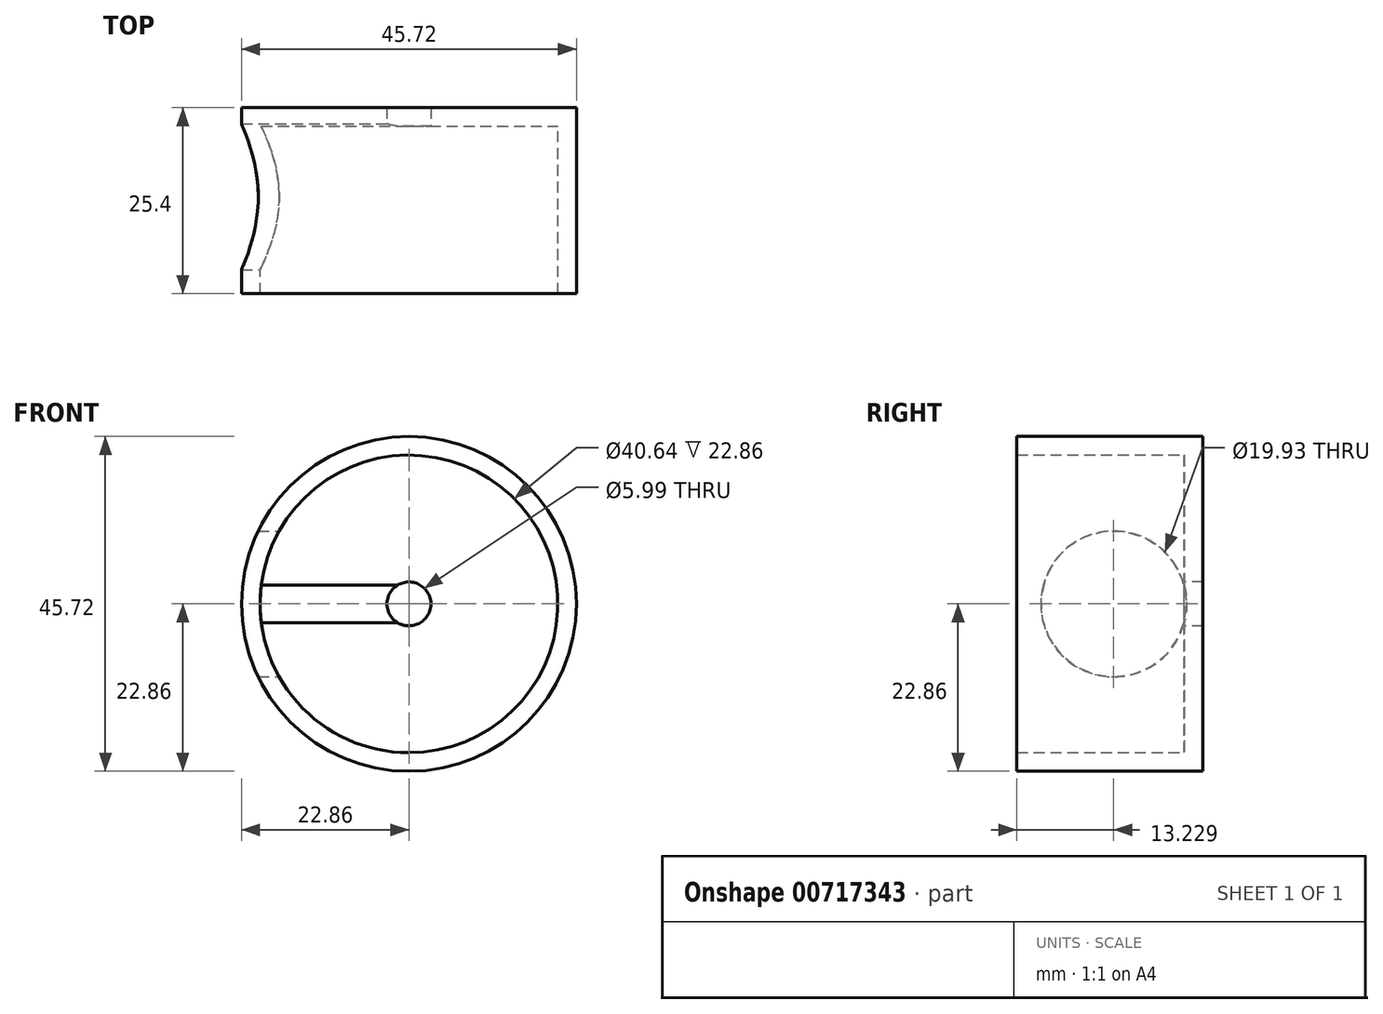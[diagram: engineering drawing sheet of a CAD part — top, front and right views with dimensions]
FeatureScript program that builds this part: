
annotation { "Feature Type Name" : "Feature", "Feature Type Description" : "" }
export const myFeature = defineFeature(function(context is Context, id is Id, definition is map)
    precondition{}
    {
        {
            var Q0;
            Q0=qCreatedBy(makeId("Front.planeOp"),FACE);
            var sketch = newSketch(context, id + "F0", { "sketchPlane" : qUnion([Q0])});
            skCircle(sketch, "E0", {"center": v(0, 0) * mm, "radius": 22.86 * mm});
            skSolve(sketch);
        }
        {
            var Q0;
            Q0=makeQuery(id+"F0.imprint","IMPRINT",FACE,{"disambiguationData":[TD([[makeQuery(id+"F0.imprint","IMPRINT",EDGE,{"derivedFrom":sQuery(id+"F0.wireOp",EDGE,"E0")}),1.0]])]});
            extrude(context, id + "F1", {"entities" : qUnion([Q0]), "depth" : 25.4 * mm, "offsetDistance" : 25.4 * mm});
        }
        {
            var Q0;
            Q0=makeQuery(id+"F1.opExtrude","CAP_FACE",FACE,{"disambiguationData":[OSD([sQuery(id+"F0.wireOp",EDGE,"E0")])],"isStart":false});
            shell(context, id + "F2", {"entities" : qUnion([Q0]), "thickness" : 2.54 * mm});
        }
        {
            var Q0;
            {var subQ0=sQuery(id+"F0.wireOp",EDGE,"E0");Q0=makeQuery(id+"F2.opShell","OFFSET_FACE",FACE,{"disambiguationData":[OSD([subQ0]),TDD([makeQuery(id+"F1.opExtrude","CAP_FACE",FACE,{"disambiguationData":[OSD([subQ0])],"isStart":true})])]});}
            var sketch = newSketch(context, id + "F3", { "sketchPlane" : qUnion([Q0])});
            skCircle(sketch, "E1", {"center": v(0, 0) * mm, "radius": 3 * mm});
            skSolve(sketch);
        }
        {
            var Q0;
            Q0=makeQuery(id+"F3.imprint","IMPRINT",FACE,{"disambiguationData":[TD([[makeQuery(id+"F3.imprint","IMPRINT",EDGE,{"derivedFrom":sQuery(id+"F3.wireOp",EDGE,"E1")}),1.0]])]});
            extrude(context, id + "F4", {"entities" : qUnion([Q0]), "operationType" : NewBodyOperationType.REMOVE, "endBound" : BoundingType.SYMMETRIC, "oppositeDirection" : true, "depth" : 25.4 * mm, "offsetDistance" : 25.4 * mm});
        }
        {
            var Q0;
            Q0=qCreatedBy(makeId("Right.planeOp"),FACE);
            var sketch = newSketch(context, id + "F5", { "sketchPlane" : qUnion([Q0])});
            skCircle(sketch, "E2", {"center": v(-12.17, 0) * mm, "radius": 9.96 * mm});
            skSolve(sketch);
        }
        {
            var Q0;
            Q0 = qSketchRegion(id + "F5", true);
            extrude(context, id + "F6", {"entities" : qUnion([Q0]), "operationType" : NewBodyOperationType.REMOVE, "endBound" : BoundingType.THROUGH_ALL, "oppositeDirection" : true, "depth" : 25.4 * mm, "offsetDistance" : 25.4 * mm});
        }
    });
